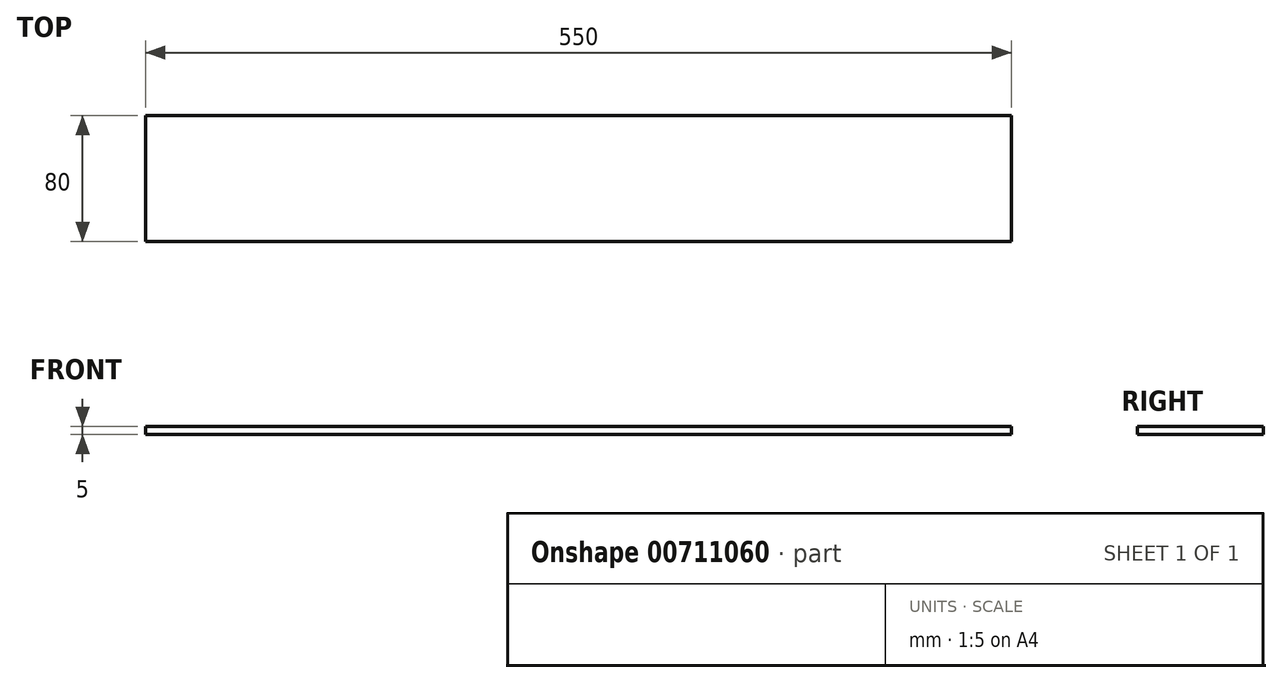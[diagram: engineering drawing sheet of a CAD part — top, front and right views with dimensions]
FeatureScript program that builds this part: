
annotation { "Feature Type Name" : "Feature", "Feature Type Description" : "" }
export const myFeature = defineFeature(function(context is Context, id is Id, definition is map)
    precondition{}
    {
        {
            var Q0;
            Q0=qCreatedBy(makeId("Top.planeOp"),FACE);
            var sketch = newSketch(context, id + "F0", { "sketchPlane" : qUnion([Q0])});
            skLineSegment(sketch, "E0.bottom", {"start": v(-275, 40) * mm, "end": v(275, 40) * mm});
            skLineSegment(sketch, "E0.top", {"start": v(-275, -40) * mm, "end": v(275, -40) * mm});
            skLineSegment(sketch, "E0.left", {"start": v(-275, 40) * mm, "end": v(-275, -40) * mm});
            skLineSegment(sketch, "E0.right", {"start": v(275, 40) * mm, "end": v(275, -40) * mm});
            skPoint(sketch, "E0.middle", {"position": v(0, 0) * mm});
            skSolve(sketch);
        }
        {
            var Q0;
            Q0=makeQuery(id+"F0.imprint","IMPRINT",FACE,{"disambiguationData":[TD([[makeQuery(id+"F0.imprint","IMPRINT",EDGE,{"derivedFrom":sQuery(id+"F0.wireOp",EDGE,"E0.bottom")}),-1.0]])]});
            extrude(context, id + "F1", {"entities" : qUnion([Q0]), "depth" : 5 * mm, "offsetDistance" : 25.4 * mm});
        }
    });
